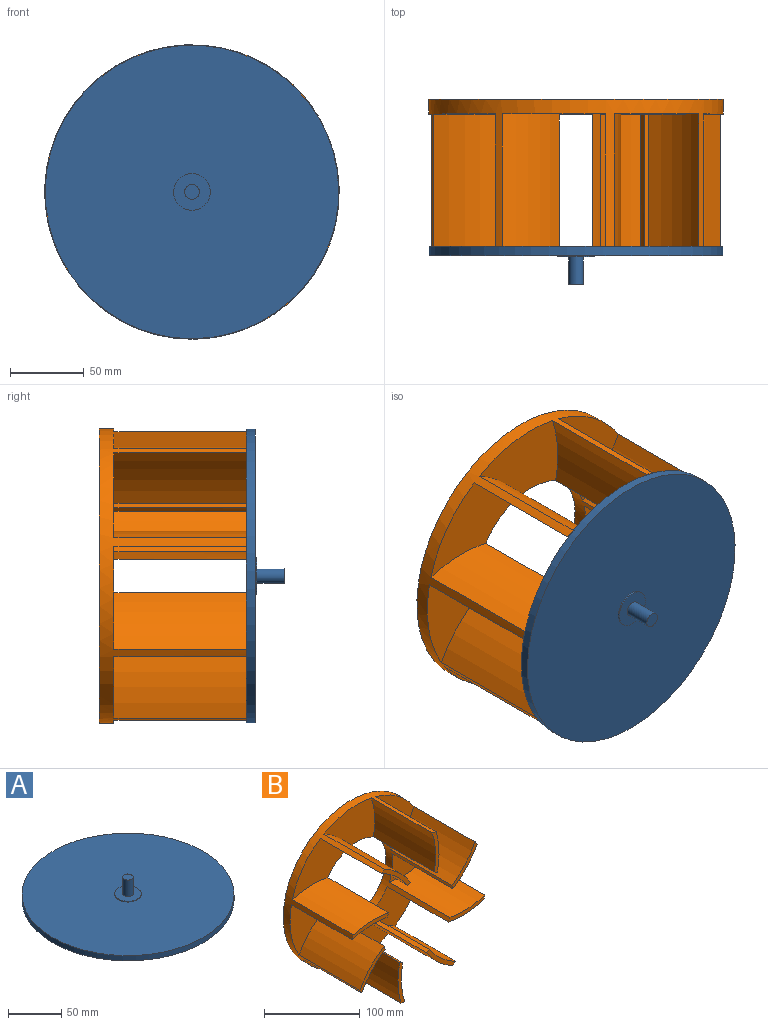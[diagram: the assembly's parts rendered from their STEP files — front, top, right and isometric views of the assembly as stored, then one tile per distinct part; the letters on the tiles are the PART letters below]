
ASSEMBLY  parts=2 mates=1
PART A: 7 faces, bbox 199.4x199.4x26 mm
  f0: cylinder r=12.5mm len=25mm, axis (0,0,-1), area 78.5mm2, adj f1,f6
  f1: plane 199.43x199.43mm, normal (0,0,1), area 30747.7mm2, adj f0,f2
  f2: cylinder r=99.72mm len=199.43mm, axis (0,0,-1), area 3759.2mm2, adj f1,f3
  f3: plane 199.43x199.43mm, normal (0,0,-1), area 31238.4mm2, adj f2
  f4: plane 10x10mm, normal (0,0,1), area 78.5mm2, adj f5
  f5: cylinder r=5mm len=19mm, axis (0,0,-1), area 596.9mm2, adj f4,f6
  f6: plane 25x25mm, normal (0,0,1), area 412.2mm2, adj f0,f5
PART B: 35 faces, bbox 200x100x200 mm
  f0: cylinder r=100mm len=90mm, axis (0,1,0), area 4690.4mm2, adj f1,f3,f4,f34
  f1: cylinder r=52mm len=104mm, axis (0,1,0), area 7043.8mm2, adj f0,f2,f4,f5,f6,f7,f8,f9
  f2: cylinder r=105mm len=90mm, axis (0,1,0), area 4795.3mm2, adj f1,f3,f4,f28
  f3: cylinder r=100mm len=200mm, axis (0,1,0), area 10475.9mm2, adj f0,f2,f4,f5,f6,f7,f8,f9
  f4: plane 43.57x37.28mm, normal (0,-1,0), area 263.4mm2, adj f0,f1,f2,f3
  f5: plane 200x200mm, normal (0,1,0), area 22921.1mm2, adj f1,f3
  f6: cylinder r=105mm len=90mm, axis (0,1,0), area 4795.3mm2, adj f1,f3,f8,f34
  f7: cylinder r=100mm len=90mm, axis (0,1,0), area 4690.4mm2, adj f1,f3,f8,f33
  f8: plane 54.02x10.06mm, normal (0,-1,0), area 263.4mm2, adj f1,f3,f6,f7
  f9: cylinder r=100mm len=90mm, axis (0,1,0), area 4690.4mm2, adj f1,f3,f11,f32
  f10: cylinder r=105mm len=90mm, axis (0,1,0), area 4795.3mm2, adj f1,f3,f11,f33
  f11: plane 43.57x37.28mm, normal (0,-1,0), area 263.4mm2, adj f1,f3,f9,f10
  f12: cylinder r=100mm len=90mm, axis (0,1,0), area 4690.4mm2, adj f1,f3,f14,f31
  f13: cylinder r=105mm len=90mm, axis (0,1,0), area 4795.3mm2, adj f1,f3,f14,f32
  f14: plane 54.02x10.06mm, normal (0,-1,0), area 263.4mm2, adj f1,f3,f12,f13
  f15: cylinder r=100mm len=90mm, axis (0,1,0), area 4690.4mm2, adj f1,f3,f17,f30
  f16: cylinder r=105mm len=90mm, axis (0,1,0), area 4795.3mm2, adj f1,f3,f17,f31
  f17: plane 43.57x37.28mm, normal (0,-1,0), area 263.4mm2, adj f1,f3,f15,f16
  f18: cylinder r=100mm len=90mm, axis (0,1,0), area 4690.4mm2, adj f1,f3,f20,f29
  f19: cylinder r=105mm len=90mm, axis (0,1,0), area 4795.3mm2, adj f1,f3,f20,f30
  f20: plane 54.02x10.06mm, normal (0,-1,0), area 263.4mm2, adj f1,f3,f18,f19
  f21: cylinder r=100mm len=90mm, axis (0,1,0), area 4690.4mm2, adj f1,f3,f23,f27
  f22: cylinder r=105mm len=90mm, axis (0,1,0), area 4795.3mm2, adj f1,f3,f23,f29
  f23: plane 43.57x37.28mm, normal (0,-1,0), area 263.4mm2, adj f1,f3,f21,f22
  f24: cylinder r=100mm len=90mm, axis (0,1,0), area 4690.4mm2, adj f1,f3,f26,f28
  f25: cylinder r=105mm len=90mm, axis (0,1,0), area 4795.3mm2, adj f1,f3,f26,f27
  f26: plane 54.02x10.06mm, normal (0,-1,0), area 263.4mm2, adj f1,f3,f24,f25
  f27: plane 80.19x57.64mm, normal (0,-1,0), area 2601.7mm2, adj f1,f3,f21,f25
  f28: plane 75.28x53.52mm, normal (0,-1,0), area 2601.7mm2, adj f1,f2,f3,f24
  f29: plane 75.28x53.52mm, normal (0,-1,0), area 2601.7mm2, adj f1,f3,f18,f22
  f30: plane 80.19x57.64mm, normal (0,-1,0), area 2601.7mm2, adj f1,f3,f15,f19
  f31: plane 75.28x53.52mm, normal (0,-1,0), area 2601.7mm2, adj f1,f3,f12,f16
  f32: plane 80.19x57.64mm, normal (0,-1,0), area 2601.7mm2, adj f1,f3,f9,f13
  f33: plane 75.28x53.52mm, normal (0,-1,0), area 2601.7mm2, adj f1,f3,f7,f10
  f34: plane 80.19x57.64mm, normal (0,-1,0), area 2601.7mm2, adj f0,f1,f3,f6
PLACE A rot(axis=(0.58,-0.58,0.58),120deg) t=(-70.65,-96.49,-21.84)mm
PLACE B t=(-70.65,13.51,27.87)mm
MATE fastened A.f0 <-> B.f1  axis (0,1,0) through (-70.65,-86.49,27.87)mm
